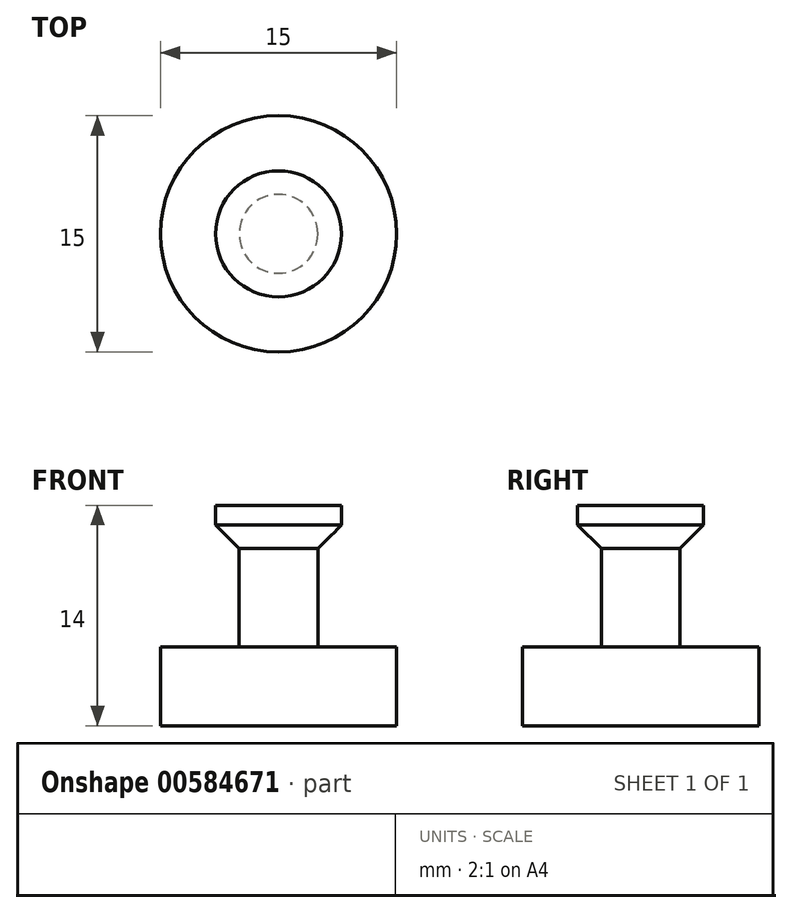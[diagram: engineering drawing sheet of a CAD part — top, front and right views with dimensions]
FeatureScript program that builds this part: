
annotation { "Feature Type Name" : "Feature", "Feature Type Description" : "" }
export const myFeature = defineFeature(function(context is Context, id is Id, definition is map)
    precondition{}
    {
        {
            assignVariable(context, id + "F0", {"name" : "screen_thickness", "anyValue" : 5});
        }
        {
            assignVariable(context, id + "F1", {"name" : "main_thickness", "anyValue" : 5});
        }
        {
            assignVariable(context, id + "F2", {"name" : "top_diameter", "anyValue" : 8});
        }
        {
            assignVariable(context, id + "F3", {"name" : "top_thickness", "anyValue" : 2});
        }
        {
            assignVariable(context, id + "F4", {"name" : "post_height", "anyValue" : getVariable(context, 'screen_thickness') + getVariable(context, 'main_thickness') + getVariable(context, 'top_thickness')});
        }
        {
            assignVariable(context, id + "F5", {"name" : "post_diameter", "anyValue" : 5});
        }
        {
            var Q0;
            Q0=qCreatedBy(makeId("Top.planeOp"),FACE);
            var sketch = newSketch(context, id + "F6", { "sketchPlane" : qUnion([Q0])});
            skCircle(sketch, "E0", {"center": v(0, 0) * mm, "radius": 7.5 * mm});
            skCircle(sketch, "E1", {"center": v(0, 0) * mm, "radius": 2.5 * mm});
            skSolve(sketch);
        }
        {
            var Q0;
            Q0=makeQuery(id+"F6.imprint","IMPRINT",FACE,{"disambiguationData":[TD([[makeQuery(id+"F6.imprint","IMPRINT",EDGE,{"derivedFrom":sQuery(id+"F6.wireOp",EDGE,"E1")}),1.0]])]});
            var Q1;
            Q1=sQuery(id+"F6.wireOp",EDGE,"E1");
            extrude(context, id + "F7", {"entities" : qUnion([Q0]), "surfaceEntities" : qUnion([Q1]), "depth" : (getVariable(context, 'post_height')) * mm, "offsetDistance" : 25 * mm});
        }
        {
            var Q0;
            Q0 = qSketchRegion(id + "F6", true);
            extrude(context, id + "F8", {"entities" : qUnion([Q0]), "operationType" : NewBodyOperationType.ADD, "depth" : (getVariable(context, 'main_thickness')) * mm, "offsetDistance" : 25 * mm});
        }
        {
            var Q0;
            Q0=makeQuery(id+"F7.opExtrude","CAP_FACE",FACE,{"disambiguationData":[OSD([sQuery(id+"F6.wireOp",EDGE,"E1")])],"isStart":false});
            var sketch = newSketch(context, id + "F9", { "sketchPlane" : qUnion([Q0])});
            skCircle(sketch, "E2", {"center": v(0, 0) * mm, "radius": 4 * mm});
            skSolve(sketch);
        }
        {
            var Q0;
            Q0=makeQuery(id+"F9.imprint","IMPRINT",FACE,{"disambiguationData":[TD([[makeQuery(id+"F9.imprint","IMPRINT",EDGE,{"derivedFrom":makeQuery(id+"F7.opExtrude","CAP_EDGE",EDGE,{"disambiguationData":[OSD([sQuery(id+"F6.wireOp",EDGE,"E1")])],"isStart":false})}),1.0]])]});
            var Q1;
            Q1=makeQuery(id+"F9.imprint","IMPRINT",FACE,{"disambiguationData":[TD([[makeQuery(id+"F9.imprint","IMPRINT",EDGE,{"derivedFrom":sQuery(id+"F9.wireOp",EDGE,"E2")}),1.0]])]});
            extrude(context, id + "F10", {"entities" : qUnion([Q0, Q1]), "operationType" : NewBodyOperationType.ADD, "depth" : (getVariable(context, 'top_thickness')) * mm, "offsetDistance" : 25 * mm});
        }
        {
            var Q0;
            Q0=makeQuery(id+"F10.opExtrude","CAP_FACE",FACE,{"disambiguationData":[OSD([sQuery(id+"F9.wireOp",EDGE,"E2")])],"isStart":true});
            chamfer(context, id + "F11", {"entities" : qUnion([Q0]), "width" : (0.25 * (getVariable(context, 'top_diameter') - getVariable(context, 'post_diameter'))) * mm, "tangentPropagation" : true});
        }
    });
